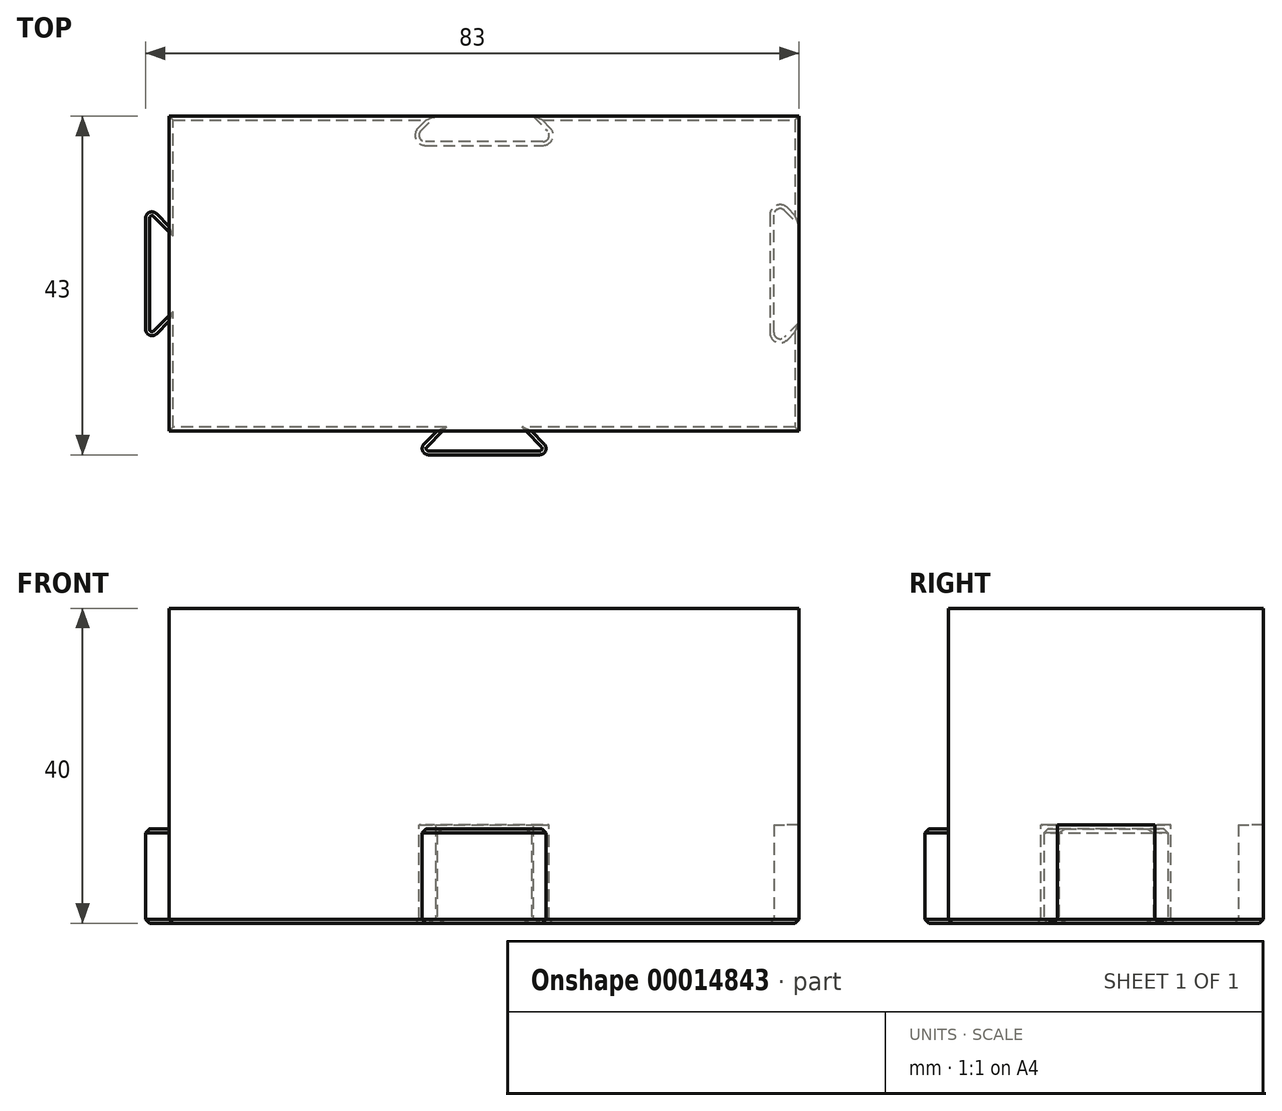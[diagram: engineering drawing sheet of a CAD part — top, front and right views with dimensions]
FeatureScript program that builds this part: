
annotation { "Feature Type Name" : "Feature", "Feature Type Description" : "" }
export const myFeature = defineFeature(function(context is Context, id is Id, definition is map)
    precondition{}
    {
        {
            var Q0;
            Q0=qCreatedBy(makeId("Top.planeOp"),FACE);
            var sketch = newSketch(context, id + "F0", { "sketchPlane" : qUnion([Q0])});
            skLineSegment(sketch, "E0.bottom", {"start": v(0, 0) * mm, "end": v(80, 0) * mm});
            skLineSegment(sketch, "E0.top", {"start": v(0, 40) * mm, "end": v(80, 40) * mm});
            skLineSegment(sketch, "E0.left", {"start": v(0, 0) * mm, "end": v(0, 40) * mm});
            skLineSegment(sketch, "E0.right", {"start": v(80, 0) * mm, "end": v(80, 40) * mm});
            skLineSegment(sketch, "E1", {"start": v(0, 20) * mm, "end": v(80, 20) * mm, "construction": true});
            skLineSegment(sketch, "E2", {"start": v(40, 40) * mm, "end": v(40, 0) * mm, "construction": true});
            skLineSegment(sketch, "E3", {"start": v(34, 0) * mm, "end": v(31, -3) * mm});
            skLineSegment(sketch, "E4", {"start": v(31, -3) * mm, "end": v(49, -3) * mm});
            skLineSegment(sketch, "E5", {"start": v(49, -3) * mm, "end": v(46, 0) * mm});
            skLineSegment(sketch, "E6", {"start": v(46.2, 40) * mm, "end": v(49.4, 36.8) * mm});
            skLineSegment(sketch, "E7", {"start": v(49.4, 36.8) * mm, "end": v(30.6, 36.8) * mm});
            skLineSegment(sketch, "E8", {"start": v(30.6, 36.8) * mm, "end": v(33.8, 40) * mm});
            skLineSegment(sketch, "E9", {"start": v(0, 14) * mm, "end": v(-3, 11) * mm});
            skLineSegment(sketch, "E10", {"start": v(-3, 11) * mm, "end": v(-3, 29) * mm});
            skLineSegment(sketch, "E11", {"start": v(-3, 29) * mm, "end": v(0, 26) * mm});
            skLineSegment(sketch, "E12", {"start": v(80, 13.8) * mm, "end": v(76.8, 10.6) * mm});
            skLineSegment(sketch, "E13", {"start": v(76.8, 10.6) * mm, "end": v(76.8, 29.4) * mm});
            skLineSegment(sketch, "E14", {"start": v(76.8, 29.4) * mm, "end": v(80, 26.2) * mm});
            skSolve(sketch);
        }
        {
            var Q0;
            {var subQ1=sQuery(id+"F0.wireOp",EDGE,"E6");Q0=makeQuery(id+"F0.imprint","IMPRINT",FACE,{"disambiguationData":[TD([[makeQuery(id+"F0.imprint","IMPRINT",EDGE,{"derivedFrom":subQ1}),-1.0]])]});}
            var Q1;
            {var subQ1=sQuery(id+"F0.wireOp",EDGE,"E12");Q1=makeQuery(id+"F0.imprint","IMPRINT",FACE,{"disambiguationData":[TD([[makeQuery(id+"F0.imprint","IMPRINT",EDGE,{"derivedFrom":subQ1}),-1.0]])]});}
            var Q2;
            {var subQ8=sQuery(id+"F0.wireOp",EDGE,"E6");Q2=makeQuery(id+"F0.imprint","IMPRINT",FACE,{"disambiguationData":[TD([[makeQuery(id+"F0.imprint","IMPRINT",EDGE,{"derivedFrom":subQ8}),1.0]])]});}
            extrude(context, id + "F1", {"entities" : qUnion([Q0, Q1, Q2]), "depth" : 40 * mm});
        }
        {
            var Q0;
            {var subQ1=sQuery(id+"F0.wireOp",EDGE,"E3");Q0=makeQuery(id+"F0.imprint","IMPRINT",FACE,{"disambiguationData":[TD([[makeQuery(id+"F0.imprint","IMPRINT",EDGE,{"derivedFrom":subQ1}),1.0]])]});}
            var Q1;
            {var subQ1=sQuery(id+"F0.wireOp",EDGE,"E9");Q1=makeQuery(id+"F0.imprint","IMPRINT",FACE,{"disambiguationData":[TD([[makeQuery(id+"F0.imprint","IMPRINT",EDGE,{"derivedFrom":subQ1}),-1.0]])]});}
            extrude(context, id + "F2", {"entities" : qUnion([Q0, Q1]), "operationType" : NewBodyOperationType.ADD, "depth" : 12 * mm});
        }
        {
            var Q0;
            {var subQ1=sQuery(id+"F0.wireOp",EDGE,"E6");Q0=makeQuery(id+"F0.imprint","IMPRINT",FACE,{"disambiguationData":[TD([[makeQuery(id+"F0.imprint","IMPRINT",EDGE,{"derivedFrom":subQ1}),-1.0]])]});}
            var Q1;
            {var subQ1=sQuery(id+"F0.wireOp",EDGE,"E12");Q1=makeQuery(id+"F0.imprint","IMPRINT",FACE,{"disambiguationData":[TD([[makeQuery(id+"F0.imprint","IMPRINT",EDGE,{"derivedFrom":subQ1}),-1.0]])]});}
            extrude(context, id + "F3", {"entities" : qUnion([Q0, Q1]), "operationType" : NewBodyOperationType.REMOVE, "depth" : 12.5 * mm});
        }
        {
            var Q0;
            Q0=makeQuery(id+"F3.boolean.opBoolean","COPY",EDGE,{"derivedFrom":makeQuery(id+"F3.opExtrude","SWEPT_EDGE",EDGE,{"disambiguationData":[OSD([sQuery(id+"F0.wireOp",EDGE,"E0.right"),sQuery(id+"F0.wireOp",EDGE,"E14")])]})});
            var Q1;
            Q1=makeQuery(id+"F3.boolean.opBoolean","COPY",EDGE,{"derivedFrom":makeQuery(id+"F3.opExtrude","SWEPT_EDGE",EDGE,{"disambiguationData":[OSD([sQuery(id+"F0.wireOp",EDGE,"E13"),sQuery(id+"F0.wireOp",EDGE,"E14")])]})});
            var Q2;
            Q2=makeQuery(id+"F3.boolean.opBoolean","COPY",EDGE,{"derivedFrom":makeQuery(id+"F3.opExtrude","SWEPT_EDGE",EDGE,{"disambiguationData":[OSD([sQuery(id+"F0.wireOp",EDGE,"E0.right"),sQuery(id+"F0.wireOp",EDGE,"E12")])]})});
            var Q3;
            Q3=makeQuery(id+"F2.opExtrude","SWEPT_EDGE",EDGE,{"disambiguationData":[OSD([sQuery(id+"F0.wireOp",EDGE,"E4"),sQuery(id+"F0.wireOp",EDGE,"E5")])]});
            var Q4;
            Q4=makeQuery(id+"F3.boolean.opBoolean","COPY",EDGE,{"derivedFrom":makeQuery(id+"F3.opExtrude","SWEPT_EDGE",EDGE,{"disambiguationData":[OSD([sQuery(id+"F0.wireOp",EDGE,"E12"),sQuery(id+"F0.wireOp",EDGE,"E13")])]})});
            var Q5;
            Q5=makeQuery(id+"F3.boolean.opBoolean","COPY",EDGE,{"derivedFrom":makeQuery(id+"F3.opExtrude","SWEPT_EDGE",EDGE,{"disambiguationData":[OSD([sQuery(id+"F0.wireOp",EDGE,"E0.top"),sQuery(id+"F0.wireOp",EDGE,"E8")])]})});
            var Q6;
            Q6=makeQuery(id+"F3.boolean.opBoolean","COPY",EDGE,{"derivedFrom":makeQuery(id+"F3.opExtrude","SWEPT_EDGE",EDGE,{"disambiguationData":[OSD([sQuery(id+"F0.wireOp",EDGE,"E0.top"),sQuery(id+"F0.wireOp",EDGE,"E6")])]})});
            var Q7;
            Q7=makeQuery(id+"F3.boolean.opBoolean","COPY",EDGE,{"derivedFrom":makeQuery(id+"F3.opExtrude","SWEPT_EDGE",EDGE,{"disambiguationData":[OSD([sQuery(id+"F0.wireOp",EDGE,"E7"),sQuery(id+"F0.wireOp",EDGE,"E8")])]})});
            var Q8;
            Q8=makeQuery(id+"F3.boolean.opBoolean","COPY",EDGE,{"derivedFrom":makeQuery(id+"F3.opExtrude","SWEPT_EDGE",EDGE,{"disambiguationData":[OSD([sQuery(id+"F0.wireOp",EDGE,"E6"),sQuery(id+"F0.wireOp",EDGE,"E7")])]})});
            var Q9;
            Q9=makeQuery(id+"F2.opExtrude","SWEPT_EDGE",EDGE,{"disambiguationData":[OSD([sQuery(id+"F0.wireOp",EDGE,"E10"),sQuery(id+"F0.wireOp",EDGE,"E11")])]});
            var Q10;
            Q10=makeQuery(id+"F2.opExtrude","SWEPT_EDGE",EDGE,{"disambiguationData":[OSD([sQuery(id+"F0.wireOp",EDGE,"E0.left"),sQuery(id+"F0.wireOp",EDGE,"E11")])]});
            var Q11;
            Q11=makeQuery(id+"F2.opExtrude","SWEPT_EDGE",EDGE,{"disambiguationData":[OSD([sQuery(id+"F0.wireOp",EDGE,"E0.left"),sQuery(id+"F0.wireOp",EDGE,"E9")])]});
            var Q12;
            Q12=makeQuery(id+"F2.opExtrude","SWEPT_EDGE",EDGE,{"disambiguationData":[OSD([sQuery(id+"F0.wireOp",EDGE,"E9"),sQuery(id+"F0.wireOp",EDGE,"E10")])]});
            var Q13;
            Q13=makeQuery(id+"F2.opExtrude","SWEPT_EDGE",EDGE,{"disambiguationData":[OSD([sQuery(id+"F0.wireOp",EDGE,"E3"),sQuery(id+"F0.wireOp",EDGE,"E4")])]});
            var Q14;
            Q14=makeQuery(id+"F2.opExtrude","SWEPT_EDGE",EDGE,{"disambiguationData":[OSD([sQuery(id+"F0.wireOp",EDGE,"E0.bottom"),sQuery(id+"F0.wireOp",EDGE,"E3")])]});
            var Q15;
            Q15=makeQuery(id+"F2.opExtrude","SWEPT_EDGE",EDGE,{"disambiguationData":[OSD([sQuery(id+"F0.wireOp",EDGE,"E0.bottom"),sQuery(id+"F0.wireOp",EDGE,"E5")])]});
            fillet(context, id + "F4", {"entities" : qUnion([Q0, Q1, Q2, Q3, Q4, Q5, Q6, Q7, Q8, Q9, Q10, Q11, Q12, Q13, Q14, Q15]), "radius" : .8 * mm, "tangentPropagation" : true, "allowEdgeOverflow" : false});
        }
        {
            var Q0;
            Q0=makeQuery(id+"F2.opExtrude","CAP_EDGE",EDGE,{"disambiguationData":[OSD([sQuery(id+"F0.wireOp",EDGE,"E4")])],"isStart":false});
            var Q1;
            Q1=makeQuery(id+"F2.opExtrude","CAP_EDGE",EDGE,{"disambiguationData":[OSD([sQuery(id+"F0.wireOp",EDGE,"E10")])],"isStart":false});
            chamfer(context, id + "F5", {"entities" : qUnion([Q0, Q1]), "width" : .5 * mm, "tangentPropagation" : true});
        }
        {
            var Q0;
            {var subQ0=sQuery(id+"F0.wireOp",EDGE,"E0.bottom");var subQ1=sQuery(id+"F0.wireOp",EDGE,"E0.left");Q0=makeQuery(id+"F2.boolean.opBoolean","MERGE",FACE,{"derivedFrom":[makeQuery(id+"F1.opExtrude","CAP_FACE",FACE,{"disambiguationData":[OSD([subQ0,sQuery(id+"F0.wireOp",EDGE,"E0.top"),subQ1,sQuery(id+"F0.wireOp",EDGE,"E0.right")])],"isStart":true}),makeQuery(id+"F2.opExtrude","CAP_FACE",FACE,{"disambiguationData":[OSD([subQ0,sQuery(id+"F0.wireOp",EDGE,"E3"),sQuery(id+"F0.wireOp",EDGE,"E4"),sQuery(id+"F0.wireOp",EDGE,"E5")])],"isStart":true}),makeQuery(id+"F2.opExtrude","CAP_FACE",FACE,{"disambiguationData":[OSD([subQ1,sQuery(id+"F0.wireOp",EDGE,"E9"),sQuery(id+"F0.wireOp",EDGE,"E10"),sQuery(id+"F0.wireOp",EDGE,"E11")])],"isStart":true})]});}
            chamfer(context, id + "F6", {"entities" : qUnion([Q0]), "width" : .5 * mm, "tangentPropagation" : true});
        }
    });
